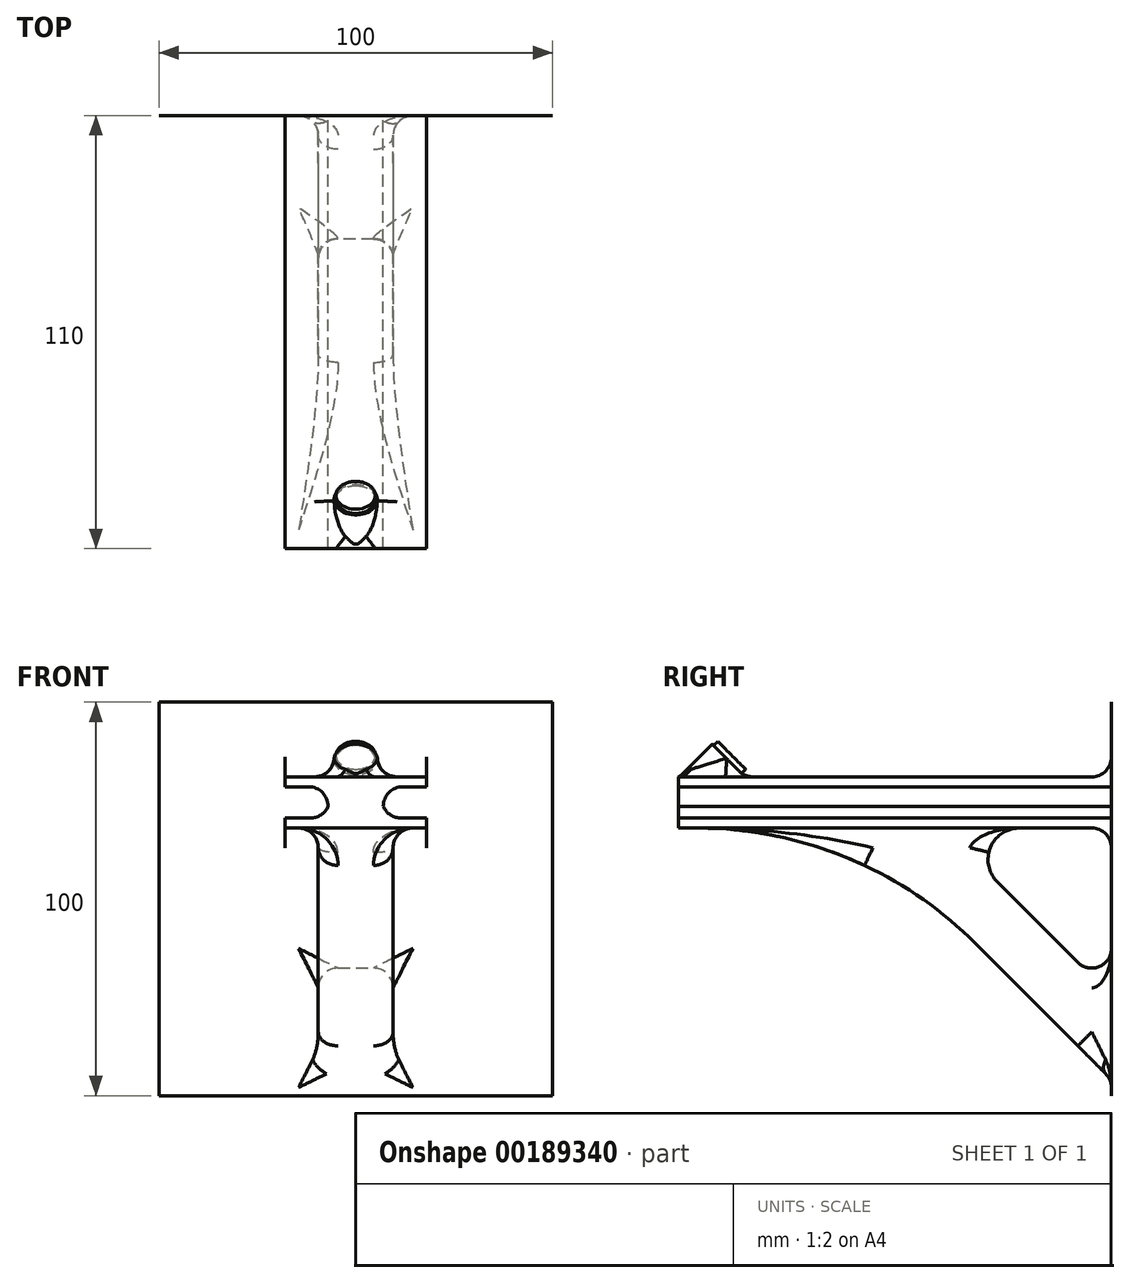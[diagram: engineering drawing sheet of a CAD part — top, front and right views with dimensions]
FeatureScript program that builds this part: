
annotation { "Feature Type Name" : "Feature", "Feature Type Description" : "" }
export const myFeature = defineFeature(function(context is Context, id is Id, definition is map)
    precondition{}
    {
        {
            var Q0;
            Q0=qCreatedBy(makeId("Front.planeOp"),FACE);
            var sketch = newSketch(context, id + "F0", { "sketchPlane" : qUnion([Q0])});
            skLineSegment(sketch, "E0", {"start": v(0, 10) * mm, "end": v(-50, 10) * mm});
            skLineSegment(sketch, "E1", {"start": v(-50, 10) * mm, "end": v(-50, -90) * mm});
            skLineSegment(sketch, "E2", {"start": v(-50, -90) * mm, "end": v(0, -90) * mm});
            skLineSegment(sketch, "E3.MirrorCS", {"start": v(0, 10) * mm, "end": v(50, 10) * mm});
            skLineSegment(sketch, "E4.MirrorCS", {"start": v(50, 10) * mm, "end": v(50, -90) * mm});
            skLineSegment(sketch, "E5.MirrorCS", {"start": v(50, -90) * mm, "end": v(0, -90) * mm});
            skLineSegment(sketch, "E6", {"start": v(0, -9) * mm, "end": v(-18, -9) * mm});
            skLineSegment(sketch, "E7", {"start": v(-18, -9) * mm, "end": v(-18, -11.5) * mm});
            skLineSegment(sketch, "E8", {"start": v(-18, -11.5) * mm, "end": v(-7, -11.5) * mm});
            skLineSegment(sketch, "E9", {"start": v(-7, -11.5) * mm, "end": v(-7, -19.5) * mm});
            skLineSegment(sketch, "E10", {"start": v(-7, -19.5) * mm, "end": v(-18, -19.5) * mm});
            skLineSegment(sketch, "E11", {"start": v(-18, -19.5) * mm, "end": v(-18, -22) * mm});
            skLineSegment(sketch, "E12", {"start": v(-18, -22) * mm, "end": v(0, -22) * mm});
            skLineSegment(sketch, "E13.MirrorCS", {"start": v(0, -9) * mm, "end": v(18, -9) * mm});
            skLineSegment(sketch, "E14.MirrorCS", {"start": v(18, -9) * mm, "end": v(18, -11.5) * mm});
            skLineSegment(sketch, "E15.MirrorCS", {"start": v(18, -11.5) * mm, "end": v(7, -11.5) * mm});
            skLineSegment(sketch, "E16.MirrorCS", {"start": v(7, -11.5) * mm, "end": v(7, -19.5) * mm});
            skLineSegment(sketch, "E17.MirrorCS", {"start": v(7, -19.5) * mm, "end": v(18, -19.5) * mm});
            skLineSegment(sketch, "E18.MirrorCS", {"start": v(18, -22) * mm, "end": v(0, -22) * mm});
            skLineSegment(sketch, "E19.MirrorCS", {"start": v(18, -19.5) * mm, "end": v(18, -22) * mm});
            skSolve(sketch);
        }
        {
            var Q0;
            Q0 = qSketchRegion(id + "F0", true);
            var Q1;
            Q1=makeQuery(id+"F0.imprint","IMPRINT",FACE,{"disambiguationData":[TD([[makeQuery(id+"F0.imprint","IMPRINT",EDGE,{"derivedFrom":sQuery(id+"F0.wireOp",EDGE,"E6")}),1.0]])]});
            extrude(context, id + "F1", {"entities" : qUnion([Q0, Q1]), "depth" : 0.01 * mm});
        }
        {
            var Q0;
            Q0=makeQuery(id+"F0.imprint","IMPRINT",FACE,{"disambiguationData":[TD([[makeQuery(id+"F0.imprint","IMPRINT",EDGE,{"derivedFrom":sQuery(id+"F0.wireOp",EDGE,"E6")}),1.0]])]});
            extrude(context, id + "F2", {"entities" : qUnion([Q0]), "operationType" : NewBodyOperationType.ADD, "depth" : 110 * mm});
        }
        {
            var Q0;
            Q0=qCreatedBy(makeId("Right.planeOp"),FACE);
            var sketch = newSketch(context, id + "F3", { "sketchPlane" : qUnion([Q0])});
            skLineSegment(sketch, "E20", {"start": v(0, -21.48) * mm, "end": v(-100, -21.48) * mm});
            skLineSegment(sketch, "E21", {"start": v(0, -64.67) * mm, "end": v(-43.2, -21.48) * mm});
            skLineSegment(sketch, "E22", {"start": v(0, -85.89) * mm, "end": v(-64.4, -21.48) * mm});
            skLineSegment(sketch, "E23", {"start": v(0, -64.67) * mm, "end": v(0, -85.89) * mm});
            skPoint(sketch, "E24", {"position": v(-100, 0) * mm});
            skLineSegment(sketch, "E25", {"start": v(-29.82, -20.07) * mm, "end": v(-37.2, -27.46) * mm});
            skLineSegment(sketch, "E26", {"start": v(-100, 0) * mm, "end": v(-100, -7.07) * mm});
            skSolve(sketch);
        }
        {
            var Q0;
            {var subQ0=sQuery(id+"F3.wireOp",EDGE,"E21");Q0=makeQuery(id+"F3.imprint","IMPRINT",FACE,{"disambiguationData":[TD([[makeQuery(id+"F3.imprint","IMPRINT",EDGE,{"derivedFrom":subQ0}),1.0]])]});}
            extrude(context, id + "F4", {"entities" : qUnion([Q0]), "operationType" : NewBodyOperationType.ADD, "endBound" : BoundingType.SYMMETRIC, "depth" : 19 * mm});
        }
        {
            var Q0;
            Q0=sQuery(id+"F3.wireOp",VERTEX,"E24");
            var Q1;
            Q1=sQuery(id+"F3.wireOp",EDGE,"E25");
            cPlane(context, id + "F5", {"entities" : qUnion([Q0, Q1]), "cplaneType" : CPlaneType.LINE_POINT, "offset" : 25 * mm, "width" : 150 * mm, "height" : 150 * mm});
        }
        {
            var Q0;
            Q0=qCreatedBy(id+"F5.planeOp",FACE);
            var sketch = newSketch(context, id + "F6", { "sketchPlane" : qUnion([Q0])});
            skLineSegment(sketch, "E27", {"start": v(-5.25, 65.71) * mm, "end": v(5.78, 65.71) * mm});
            skCircle(sketch, "E28", {"center": v(0, 65.71) * mm, "radius": 5 * mm});
            skSolve(sketch);
        }
        {
            var Q0;
            {var subQ0=sQuery(id+"F6.wireOp",EDGE,"E28");var subQ1=sQuery(id+"F6.wireOp",EDGE,"E27");var subQ2=makeQuery(id+"F6.imprint","INTERSECT",VERTEX,{"disambiguationData":[OD(0.0)],"derivedFrom":[subQ1,subQ0]});Q0=makeQuery(id+"F6.imprint","IMPRINT",FACE,{"disambiguationData":[TD([[makeQuery(id+"F6.imprint","IMPRINT",EDGE,{"disambiguationData":[TD([[subQ2,-1.0]])],"derivedFrom":subQ1}),-1.0]])]});}
            var Q1;
            {var subQ0=sQuery(id+"F6.wireOp",EDGE,"E28");var subQ1=sQuery(id+"F6.wireOp",EDGE,"E27");var subQ2=makeQuery(id+"F6.imprint","INTERSECT",VERTEX,{"disambiguationData":[OD(0.0)],"derivedFrom":[subQ1,subQ0]});Q1=makeQuery(id+"F6.imprint","IMPRINT",FACE,{"disambiguationData":[TD([[makeQuery(id+"F6.imprint","IMPRINT",EDGE,{"disambiguationData":[TD([[subQ2,-1.0]])],"derivedFrom":subQ1}),1.0]])]});}
            extrude(context, id + "F7", {"entities" : qUnion([Q0, Q1]), "operationType" : NewBodyOperationType.ADD, "depth" : 5 * mm});
        }
        {
            var Q0;
            Q0=makeQuery(id+"F4.boolean.opBoolean","INTERSECT",EDGE,{"derivedFrom":[makeQuery(id+"F2.opExtrude","SWEPT_FACE",FACE,{"disambiguationData":[OSD([sQuery(id+"F0.wireOp",EDGE,"E12"),sQuery(id+"F0.wireOp",EDGE,"E18.MirrorCS")])]}),makeQuery(id+"F4.opExtrude","SWEPT_FACE",FACE,{"disambiguationData":[OSD([sQuery(id+"F3.wireOp",EDGE,"E22")])]})]});
            fillet(context, id + "F8", {"entities" : qUnion([Q0]), "radius" : 100 * mm, "tangentPropagation" : true, "allowEdgeOverflow" : false});
        }
        {
            var Q0;
            Q0=makeQuery(id+"F4.boolean.opBoolean","INTERSECT",EDGE,{"derivedFrom":[makeQuery(id+"F2.opExtrude","SWEPT_FACE",FACE,{"disambiguationData":[OSD([sQuery(id+"F0.wireOp",EDGE,"E12"),sQuery(id+"F0.wireOp",EDGE,"E18.MirrorCS")])]}),makeQuery(id+"F4.opExtrude","CAP_FACE",FACE,{"disambiguationData":[OSD([sQuery(id+"F3.wireOp",EDGE,"E20"),sQuery(id+"F3.wireOp",EDGE,"E21"),sQuery(id+"F3.wireOp",EDGE,"E22"),sQuery(id+"F3.wireOp",EDGE,"E23")])],"isStart":false})]});
            fillet(context, id + "F9", {"entities" : qUnion([Q0]), "radius" : 5 * mm, "tangentPropagation" : true, "allowEdgeOverflow" : false});
        }
        {
            var Q0;
            Q0=makeQuery(id+"F4.boolean.opBoolean","INTERSECT",EDGE,{"derivedFrom":[makeQuery(id+"F2.opExtrude","SWEPT_FACE",FACE,{"disambiguationData":[OSD([sQuery(id+"F0.wireOp",EDGE,"E12"),sQuery(id+"F0.wireOp",EDGE,"E18.MirrorCS")])]}),makeQuery(id+"F4.opExtrude","CAP_FACE",FACE,{"disambiguationData":[OSD([sQuery(id+"F3.wireOp",EDGE,"E20"),sQuery(id+"F3.wireOp",EDGE,"E21"),sQuery(id+"F3.wireOp",EDGE,"E22"),sQuery(id+"F3.wireOp",EDGE,"E23")])],"isStart":true})]});
            fillet(context, id + "F10", {"entities" : qUnion([Q0]), "radius" : 5 * mm, "tangentPropagation" : true, "allowEdgeOverflow" : false});
        }
        {
            var Q0;
            Q0=makeQuery(id+"F2.opExtrude","SWEPT_EDGE",EDGE,{"disambiguationData":[OSD([sQuery(id+"F0.wireOp",EDGE,"E8"),sQuery(id+"F0.wireOp",EDGE,"E9")])]});
            fillet(context, id + "F11", {"entities" : qUnion([Q0]), "radius" : 5 * mm, "tangentPropagation" : true, "allowEdgeOverflow" : false});
        }
        {
            var Q0;
            Q0=makeQuery(id+"F2.opExtrude","SWEPT_EDGE",EDGE,{"disambiguationData":[OSD([sQuery(id+"F0.wireOp",EDGE,"E15.MirrorCS"),sQuery(id+"F0.wireOp",EDGE,"E16.MirrorCS")])]});
            fillet(context, id + "F12", {"entities" : qUnion([Q0]), "radius" : 5 * mm, "tangentPropagation" : true, "allowEdgeOverflow" : false});
        }
        {
            var Q0;
            Q0=makeQuery(id+"F2.opExtrude","SWEPT_EDGE",EDGE,{"disambiguationData":[OSD([sQuery(id+"F0.wireOp",EDGE,"E16.MirrorCS"),sQuery(id+"F0.wireOp",EDGE,"E17.MirrorCS")])]});
            fillet(context, id + "F13", {"entities" : qUnion([Q0]), "radius" : 5 * mm, "tangentPropagation" : true, "allowEdgeOverflow" : false});
        }
        {
            var Q0;
            Q0=makeQuery(id+"F2.opExtrude","SWEPT_EDGE",EDGE,{"disambiguationData":[OSD([sQuery(id+"F0.wireOp",EDGE,"E9"),sQuery(id+"F0.wireOp",EDGE,"E10")])]});
            fillet(context, id + "F14", {"entities" : qUnion([Q0]), "radius" : 5 * mm, "tangentPropagation" : true, "allowEdgeOverflow" : false});
        }
        {
            var Q0;
            Q0=makeQuery(id+"F4.boolean.opBoolean","INTERSECT",EDGE,{"derivedFrom":[makeQuery(id+"F2.opExtrude","SWEPT_FACE",FACE,{"disambiguationData":[OSD([sQuery(id+"F0.wireOp",EDGE,"E12"),sQuery(id+"F0.wireOp",EDGE,"E18.MirrorCS")])]}),makeQuery(id+"F4.opExtrude","SWEPT_FACE",FACE,{"disambiguationData":[OSD([sQuery(id+"F3.wireOp",EDGE,"E21")])]})]});
            fillet(context, id + "F15", {"entities" : qUnion([Q0]), "radius" : 8 * mm, "tangentPropagation" : true, "allowEdgeOverflow" : false});
        }
        {
            var Q0;
            Q0=qCreatedBy(id+"F5.planeOp",FACE);
            cPlane(context, id + "F16", {"entities" : qUnion([Q0]), "cplaneType" : CPlaneType.OFFSET, "offset" : 1.5 * mm, "width" : 150 * mm, "height" : 150 * mm});
        }
        {
            var Q0;
            Q0=qCreatedBy(id+"F16.planeOp",FACE);
            var sketch = newSketch(context, id + "F17", { "sketchPlane" : qUnion([Q0])});
            skCircle(sketch, "E29", {"center": v(0, 65.73) * mm, "radius": 5.5 * mm});
            skSolve(sketch);
        }
        {
            var Q0;
            Q0=makeQuery(id+"F17.imprint","IMPRINT",FACE,{"disambiguationData":[TD([[makeQuery(id+"F17.imprint","IMPRINT",EDGE,{"derivedFrom":sQuery(id+"F17.wireOp",EDGE,"E29")}),1.0]])]});
            extrude(context, id + "F18", {"entities" : qUnion([Q0]), "operationType" : NewBodyOperationType.ADD, "depth" : 12 * mm});
        }
        {
            var Q0;
            Q0=makeQuery(id+"F18.boolean.opBoolean","INTERSECT",EDGE,{"derivedFrom":[makeQuery(id+"F2.opExtrude","SWEPT_FACE",FACE,{"disambiguationData":[OSD([sQuery(id+"F0.wireOp",EDGE,"E6"),sQuery(id+"F0.wireOp",EDGE,"E13.MirrorCS")])]}),makeQuery(id+"F18.opExtrude","SWEPT_FACE",FACE,{"disambiguationData":[OSD([sQuery(id+"F17.wireOp",EDGE,"E29")])]})]});
            fillet(context, id + "F19", {"entities" : qUnion([Q0]), "radius" : 5 * mm, "tangentPropagation" : true, "allowEdgeOverflow" : false});
        }
        {
            var Q0;
            Q0=makeQuery(id+"F2.boolean.opBoolean","INTERSECT",EDGE,{"derivedFrom":[makeQuery(id+"F1.opExtrude","CAP_FACE",FACE,{"disambiguationData":[OSD([sQuery(id+"F0.wireOp",EDGE,"E0"),sQuery(id+"F0.wireOp",EDGE,"E1"),sQuery(id+"F0.wireOp",EDGE,"E2"),sQuery(id+"F0.wireOp",EDGE,"E3.MirrorCS"),sQuery(id+"F0.wireOp",EDGE,"E4.MirrorCS"),sQuery(id+"F0.wireOp",EDGE,"E5.MirrorCS")])],"isStart":false}),makeQuery(id+"F2.opExtrude","SWEPT_FACE",FACE,{"disambiguationData":[OSD([sQuery(id+"F0.wireOp",EDGE,"E12"),sQuery(id+"F0.wireOp",EDGE,"E18.MirrorCS")])]})]});
            var Q1;
            Q1=makeQuery(id+"F2.boolean.opBoolean","INTERSECT",EDGE,{"derivedFrom":[makeQuery(id+"F1.opExtrude","CAP_FACE",FACE,{"disambiguationData":[OSD([sQuery(id+"F0.wireOp",EDGE,"E0"),sQuery(id+"F0.wireOp",EDGE,"E1"),sQuery(id+"F0.wireOp",EDGE,"E2"),sQuery(id+"F0.wireOp",EDGE,"E3.MirrorCS"),sQuery(id+"F0.wireOp",EDGE,"E4.MirrorCS"),sQuery(id+"F0.wireOp",EDGE,"E5.MirrorCS")])],"isStart":false}),makeQuery(id+"F2.opExtrude","SWEPT_FACE",FACE,{"disambiguationData":[OSD([sQuery(id+"F0.wireOp",EDGE,"E6"),sQuery(id+"F0.wireOp",EDGE,"E13.MirrorCS")])]})]});
            fillet(context, id + "F20", {"entities" : qUnion([Q0, Q1]), "radius" : 5 * mm, "tangentPropagation" : true, "allowEdgeOverflow" : false});
        }
        {
            var Q0;
            Q0=makeQuery(id+"F4.boolean.opBoolean","INTERSECT",EDGE,{"derivedFrom":[makeQuery(id+"F1.opExtrude","CAP_FACE",FACE,{"disambiguationData":[OSD([sQuery(id+"F0.wireOp",EDGE,"E0"),sQuery(id+"F0.wireOp",EDGE,"E1"),sQuery(id+"F0.wireOp",EDGE,"E2"),sQuery(id+"F0.wireOp",EDGE,"E3.MirrorCS"),sQuery(id+"F0.wireOp",EDGE,"E4.MirrorCS"),sQuery(id+"F0.wireOp",EDGE,"E5.MirrorCS")])],"isStart":false}),makeQuery(id+"F4.opExtrude","CAP_FACE",FACE,{"disambiguationData":[OSD([sQuery(id+"F3.wireOp",EDGE,"E20"),sQuery(id+"F3.wireOp",EDGE,"E21"),sQuery(id+"F3.wireOp",EDGE,"E22"),sQuery(id+"F3.wireOp",EDGE,"E23")])],"isStart":false})]});
            var Q1;
            Q1=makeQuery(id+"F4.boolean.opBoolean","INTERSECT",EDGE,{"derivedFrom":[makeQuery(id+"F1.opExtrude","CAP_FACE",FACE,{"disambiguationData":[OSD([sQuery(id+"F0.wireOp",EDGE,"E0"),sQuery(id+"F0.wireOp",EDGE,"E1"),sQuery(id+"F0.wireOp",EDGE,"E2"),sQuery(id+"F0.wireOp",EDGE,"E3.MirrorCS"),sQuery(id+"F0.wireOp",EDGE,"E4.MirrorCS"),sQuery(id+"F0.wireOp",EDGE,"E5.MirrorCS")])],"isStart":false}),makeQuery(id+"F4.opExtrude","SWEPT_FACE",FACE,{"disambiguationData":[OSD([sQuery(id+"F3.wireOp",EDGE,"E22")])]})]});
            var Q2;
            Q2=makeQuery(id+"F4.boolean.opBoolean","INTERSECT",EDGE,{"derivedFrom":[makeQuery(id+"F1.opExtrude","CAP_FACE",FACE,{"disambiguationData":[OSD([sQuery(id+"F0.wireOp",EDGE,"E0"),sQuery(id+"F0.wireOp",EDGE,"E1"),sQuery(id+"F0.wireOp",EDGE,"E2"),sQuery(id+"F0.wireOp",EDGE,"E3.MirrorCS"),sQuery(id+"F0.wireOp",EDGE,"E4.MirrorCS"),sQuery(id+"F0.wireOp",EDGE,"E5.MirrorCS")])],"isStart":false}),makeQuery(id+"F4.opExtrude","CAP_FACE",FACE,{"disambiguationData":[OSD([sQuery(id+"F3.wireOp",EDGE,"E20"),sQuery(id+"F3.wireOp",EDGE,"E21"),sQuery(id+"F3.wireOp",EDGE,"E22"),sQuery(id+"F3.wireOp",EDGE,"E23")])],"isStart":true})]});
            var Q3;
            Q3=makeQuery(id+"F4.boolean.opBoolean","INTERSECT",EDGE,{"derivedFrom":[makeQuery(id+"F1.opExtrude","CAP_FACE",FACE,{"disambiguationData":[OSD([sQuery(id+"F0.wireOp",EDGE,"E0"),sQuery(id+"F0.wireOp",EDGE,"E1"),sQuery(id+"F0.wireOp",EDGE,"E2"),sQuery(id+"F0.wireOp",EDGE,"E3.MirrorCS"),sQuery(id+"F0.wireOp",EDGE,"E4.MirrorCS"),sQuery(id+"F0.wireOp",EDGE,"E5.MirrorCS")])],"isStart":false}),makeQuery(id+"F4.opExtrude","SWEPT_FACE",FACE,{"disambiguationData":[OSD([sQuery(id+"F3.wireOp",EDGE,"E21")])]})]});
            fillet(context, id + "F21", {"entities" : qUnion([Q0, Q1, Q2, Q3]), "radius" : 5 * mm, "tangentPropagation" : true, "allowEdgeOverflow" : false});
        }
        {
            var Q0;
            {var subQ0=sQuery(id+"F3.wireOp",EDGE,"E22");Q0=makeQuery(id+"F8.opFillet","BLEND_EDGE",EDGE,{"blendedFrom":[makeQuery(id+"F4.boolean.opBoolean","INTERSECT",EDGE,{"derivedFrom":[makeQuery(id+"F2.opExtrude","SWEPT_FACE",FACE,{"disambiguationData":[OSD([sQuery(id+"F0.wireOp",EDGE,"E12"),sQuery(id+"F0.wireOp",EDGE,"E18.MirrorCS")])]}),makeQuery(id+"F4.opExtrude","SWEPT_FACE",FACE,{"disambiguationData":[OSD([subQ0])]})]}),makeQuery(id+"F4.opExtrude","CAP_FACE",FACE,{"disambiguationData":[OSD([sQuery(id+"F3.wireOp",EDGE,"E20"),sQuery(id+"F3.wireOp",EDGE,"E21"),subQ0,sQuery(id+"F3.wireOp",EDGE,"E23")])],"isStart":false})],"blendedInto":[makeQuery(id+"F4.opExtrude","CAP_FACE",FACE,{"disambiguationData":[OSD([sQuery(id+"F3.wireOp",EDGE,"E20"),sQuery(id+"F3.wireOp",EDGE,"E21"),subQ0,sQuery(id+"F3.wireOp",EDGE,"E23")])],"isStart":false})]});}
            var Q1;
            {var subQ0=sQuery(id+"F3.wireOp",EDGE,"E22");Q1=makeQuery(id+"F8.opFillet","BLEND_EDGE",EDGE,{"blendedFrom":[makeQuery(id+"F4.boolean.opBoolean","INTERSECT",EDGE,{"derivedFrom":[makeQuery(id+"F2.opExtrude","SWEPT_FACE",FACE,{"disambiguationData":[OSD([sQuery(id+"F0.wireOp",EDGE,"E12"),sQuery(id+"F0.wireOp",EDGE,"E18.MirrorCS")])]}),makeQuery(id+"F4.opExtrude","SWEPT_FACE",FACE,{"disambiguationData":[OSD([subQ0])]})]}),makeQuery(id+"F4.opExtrude","CAP_FACE",FACE,{"disambiguationData":[OSD([sQuery(id+"F3.wireOp",EDGE,"E20"),sQuery(id+"F3.wireOp",EDGE,"E21"),subQ0,sQuery(id+"F3.wireOp",EDGE,"E23")])],"isStart":true})],"blendedInto":[makeQuery(id+"F4.opExtrude","CAP_FACE",FACE,{"disambiguationData":[OSD([sQuery(id+"F3.wireOp",EDGE,"E20"),sQuery(id+"F3.wireOp",EDGE,"E21"),subQ0,sQuery(id+"F3.wireOp",EDGE,"E23")])],"isStart":true})]});}
            var Q2;
            Q2=makeQuery(id+"F4.opExtrude","CAP_EDGE",EDGE,{"disambiguationData":[OSD([sQuery(id+"F3.wireOp",EDGE,"E21")])],"isStart":false});
            var Q3;
            Q3=makeQuery(id+"F4.opExtrude","CAP_EDGE",EDGE,{"disambiguationData":[OSD([sQuery(id+"F3.wireOp",EDGE,"E21")])],"isStart":true});
            fillet(context, id + "F22", {"entities" : qUnion([Q0, Q1, Q2, Q3]), "radius" : 5 * mm, "tangentPropagation" : true, "allowEdgeOverflow" : false});
        }
    });
